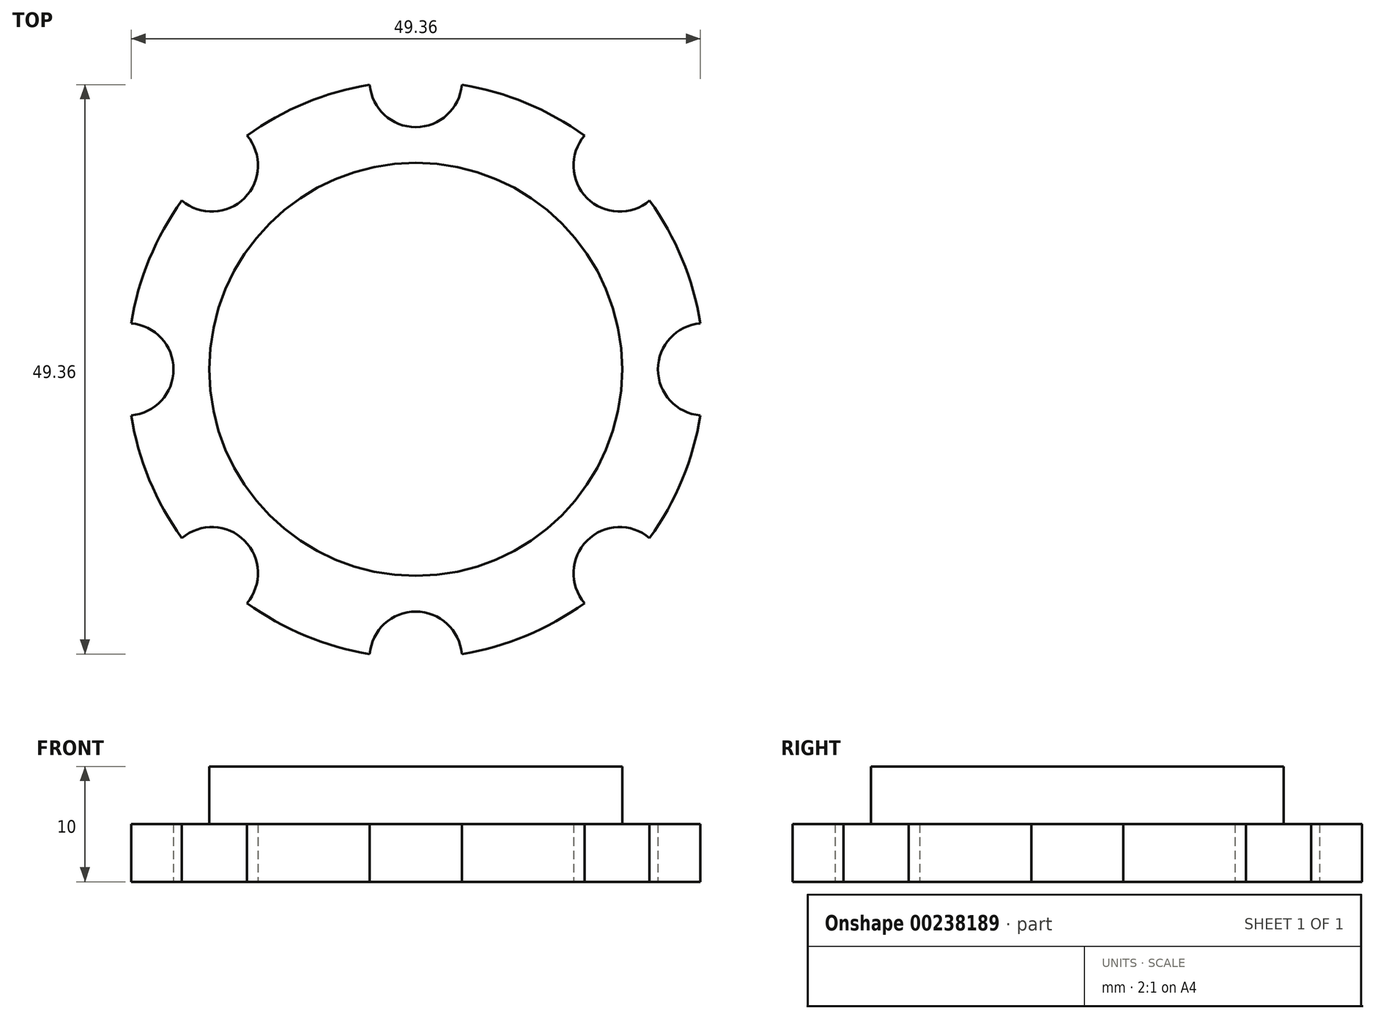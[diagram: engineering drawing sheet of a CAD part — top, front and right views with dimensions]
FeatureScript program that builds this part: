
annotation { "Feature Type Name" : "Feature", "Feature Type Description" : "" }
export const myFeature = defineFeature(function(context is Context, id is Id, definition is map)
    precondition{}
    {
        {
            var Q0;
            Q0=qCreatedBy(makeId("Top.planeOp"),FACE);
            var sketch = newSketch(context, id + "F0", { "sketchPlane" : qUnion([Q0])});
            skCircle(sketch, "E0", {"center": v(0, 0) * mm, "radius": 25 * mm});
            skSolve(sketch);
        }
        {
            var Q0;
            Q0 = qSketchRegion(id + "F0", true);
            extrude(context, id + "F1", {"entities" : qUnion([Q0]), "depth" : 5 * mm, "offsetDistance" : 25 * mm});
        }
        {
            var Q0;
            Q0=makeQuery(id+"F1.opExtrude","CAP_FACE",FACE,{"disambiguationData":[OSD([sQuery(id+"F0.wireOp",EDGE,"E0")])],"isStart":false});
            var sketch = newSketch(context, id + "F2", { "sketchPlane" : qUnion([Q0])});
            skCircle(sketch, "E1", {"center": v(0, 0) * mm, "radius": 17.9 * mm});
            skSolve(sketch);
        }
        {
            var Q0;
            Q0 = qSketchRegion(id + "F2", true);
            extrude(context, id + "F3", {"entities" : qUnion([Q0]), "operationType" : NewBodyOperationType.ADD, "depth" : 5 * mm, "offsetDistance" : 25 * mm});
        }
        {
            var Q0;
            Q0=makeQuery(id+"F1.opExtrude","CAP_FACE",FACE,{"disambiguationData":[OSD([sQuery(id+"F0.wireOp",EDGE,"E0")])],"isStart":true});
            var sketch = newSketch(context, id + "F4", { "sketchPlane" : qUnion([Q0])});
            skCircle(sketch, "E2.0", {"center": v(0, 0) * mm, "radius": 25 * mm});
            skCircle(sketch, "E3", {"center": v(0, 25) * mm, "radius": 4 * mm});
            skCircle(sketch, "E4.1.0", {"center": v(-17.68, 17.68) * mm, "radius": 4 * mm});
            skCircle(sketch, "E4.2.0", {"center": v(-25, 0) * mm, "radius": 4 * mm});
            skCircle(sketch, "E4.3.0", {"center": v(-17.68, -17.68) * mm, "radius": 4 * mm});
            skCircle(sketch, "E4.4.0", {"center": v(0, -25) * mm, "radius": 4 * mm});
            skCircle(sketch, "E4.5.0", {"center": v(17.68, -17.68) * mm, "radius": 4 * mm});
            skCircle(sketch, "E4.6.0", {"center": v(25, 0) * mm, "radius": 4 * mm});
            skCircle(sketch, "E4.7.0", {"center": v(17.68, 17.68) * mm, "radius": 4 * mm});
            skSolve(sketch);
        }
        {
            var Q0;
            {var subQ0=sQuery(id+"F4.wireOp",EDGE,"E3");var subQ1=sQuery(id+"F4.wireOp",EDGE,"E2.0");var subQ2=makeQuery(id+"F4.imprint","INTERSECT",VERTEX,{"disambiguationData":[OD(0.0)],"derivedFrom":[subQ1,subQ0]});Q0=makeQuery(id+"F4.imprint","IMPRINT",FACE,{"disambiguationData":[TD([[makeQuery(id+"F4.imprint","IMPRINT",EDGE,{"disambiguationData":[TD([[subQ2,-1.0]])],"derivedFrom":subQ1}),-1.0]])]});}
            var Q1;
            {var subQ0=sQuery(id+"F4.wireOp",EDGE,"E4.1.0");var subQ1=sQuery(id+"F4.wireOp",EDGE,"E2.0");var subQ2=makeQuery(id+"F4.imprint","INTERSECT",VERTEX,{"disambiguationData":[OD(0.0)],"derivedFrom":[subQ1,subQ0]});Q1=makeQuery(id+"F4.imprint","IMPRINT",FACE,{"disambiguationData":[TD([[makeQuery(id+"F4.imprint","IMPRINT",EDGE,{"disambiguationData":[TD([[subQ2,-1.0]])],"derivedFrom":subQ1}),-1.0]])]});}
            var Q2;
            {var subQ0=sQuery(id+"F4.wireOp",EDGE,"E4.2.0");var subQ1=sQuery(id+"F4.wireOp",EDGE,"E2.0");var subQ2=makeQuery(id+"F4.imprint","INTERSECT",VERTEX,{"disambiguationData":[OD(0.0)],"derivedFrom":[subQ1,subQ0]});Q2=makeQuery(id+"F4.imprint","IMPRINT",FACE,{"disambiguationData":[TD([[makeQuery(id+"F4.imprint","IMPRINT",EDGE,{"disambiguationData":[TD([[subQ2,-1.0]])],"derivedFrom":subQ1}),-1.0]])]});}
            var Q3;
            {var subQ0=sQuery(id+"F4.wireOp",EDGE,"E4.3.0");var subQ1=sQuery(id+"F4.wireOp",EDGE,"E2.0");var subQ2=makeQuery(id+"F4.imprint","INTERSECT",VERTEX,{"disambiguationData":[OD(0.0)],"derivedFrom":[subQ1,subQ0]});Q3=makeQuery(id+"F4.imprint","IMPRINT",FACE,{"disambiguationData":[TD([[makeQuery(id+"F4.imprint","IMPRINT",EDGE,{"disambiguationData":[TD([[subQ2,-1.0]])],"derivedFrom":subQ1}),-1.0]])]});}
            var Q4;
            {var subQ0=sQuery(id+"F4.wireOp",EDGE,"E4.4.0");var subQ1=sQuery(id+"F4.wireOp",EDGE,"E2.0");var subQ2=makeQuery(id+"F4.imprint","INTERSECT",VERTEX,{"disambiguationData":[OD(0.0)],"derivedFrom":[subQ1,subQ0]});Q4=makeQuery(id+"F4.imprint","IMPRINT",FACE,{"disambiguationData":[TD([[makeQuery(id+"F4.imprint","IMPRINT",EDGE,{"disambiguationData":[TD([[subQ2,-1.0]])],"derivedFrom":subQ1}),-1.0]])]});}
            var Q5;
            {var subQ0=sQuery(id+"F4.wireOp",EDGE,"E4.5.0");var subQ1=sQuery(id+"F4.wireOp",EDGE,"E2.0");var subQ2=makeQuery(id+"F4.imprint","INTERSECT",VERTEX,{"disambiguationData":[OD(0.0)],"derivedFrom":[subQ1,subQ0]});Q5=makeQuery(id+"F4.imprint","IMPRINT",FACE,{"disambiguationData":[TD([[makeQuery(id+"F4.imprint","IMPRINT",EDGE,{"disambiguationData":[TD([[subQ2,-1.0]])],"derivedFrom":subQ1}),-1.0]])]});}
            var Q6;
            {var subQ0=sQuery(id+"F4.wireOp",EDGE,"E4.6.0");var subQ1=sQuery(id+"F4.wireOp",EDGE,"E2.0");var subQ2=makeQuery(id+"F4.imprint","INTERSECT",VERTEX,{"disambiguationData":[OD(0.0)],"derivedFrom":[subQ1,subQ0]});Q6=makeQuery(id+"F4.imprint","IMPRINT",FACE,{"disambiguationData":[TD([[makeQuery(id+"F4.imprint","IMPRINT",EDGE,{"disambiguationData":[TD([[subQ2,1.0]])],"derivedFrom":subQ1}),-1.0]])]});}
            var Q7;
            {var subQ0=sQuery(id+"F4.wireOp",EDGE,"E4.7.0");var subQ1=sQuery(id+"F4.wireOp",EDGE,"E2.0");var subQ2=makeQuery(id+"F4.imprint","INTERSECT",VERTEX,{"disambiguationData":[OD(0.0)],"derivedFrom":[subQ1,subQ0]});Q7=makeQuery(id+"F4.imprint","IMPRINT",FACE,{"disambiguationData":[TD([[makeQuery(id+"F4.imprint","IMPRINT",EDGE,{"disambiguationData":[TD([[subQ2,-1.0]])],"derivedFrom":subQ1}),-1.0]])]});}
            extrude(context, id + "F5", {"entities" : qUnion([Q0, Q1, Q2, Q3, Q4, Q5, Q6, Q7]), "operationType" : NewBodyOperationType.REMOVE, "oppositeDirection" : true, "depth" : 25 * mm, "offsetDistance" : 25 * mm});
        }
    });
